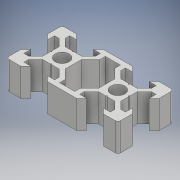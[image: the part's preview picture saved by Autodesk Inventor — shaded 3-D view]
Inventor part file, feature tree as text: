
AUTODESK INVENTOR PART (.ipt)
format: ipt  version: 2018 (Build 220112000, 112)  size: 204,288 bytes
history: native  units: mm
features: other x1, extrude x1, sketch x1
ambient origin geometry x8: Origin, YZ Plane, XZ Plane, XY Plane, X Axis, Y Axis, Z Axis, Center Point
bodies: Body1 (feature_tree)
feature tree (3):
  other  "Sólido1"
  extrude  "Extrusão1"  [1 undecoded]
  sketch  "Esboço1"  dims[d0=10.0mm d1=0.0mm]
note: 1 required parameter value undecoded (feature->parameter linkage not recoverable at this tier; creation-order binding heuristic only, values carry confidence <= 0.55)
